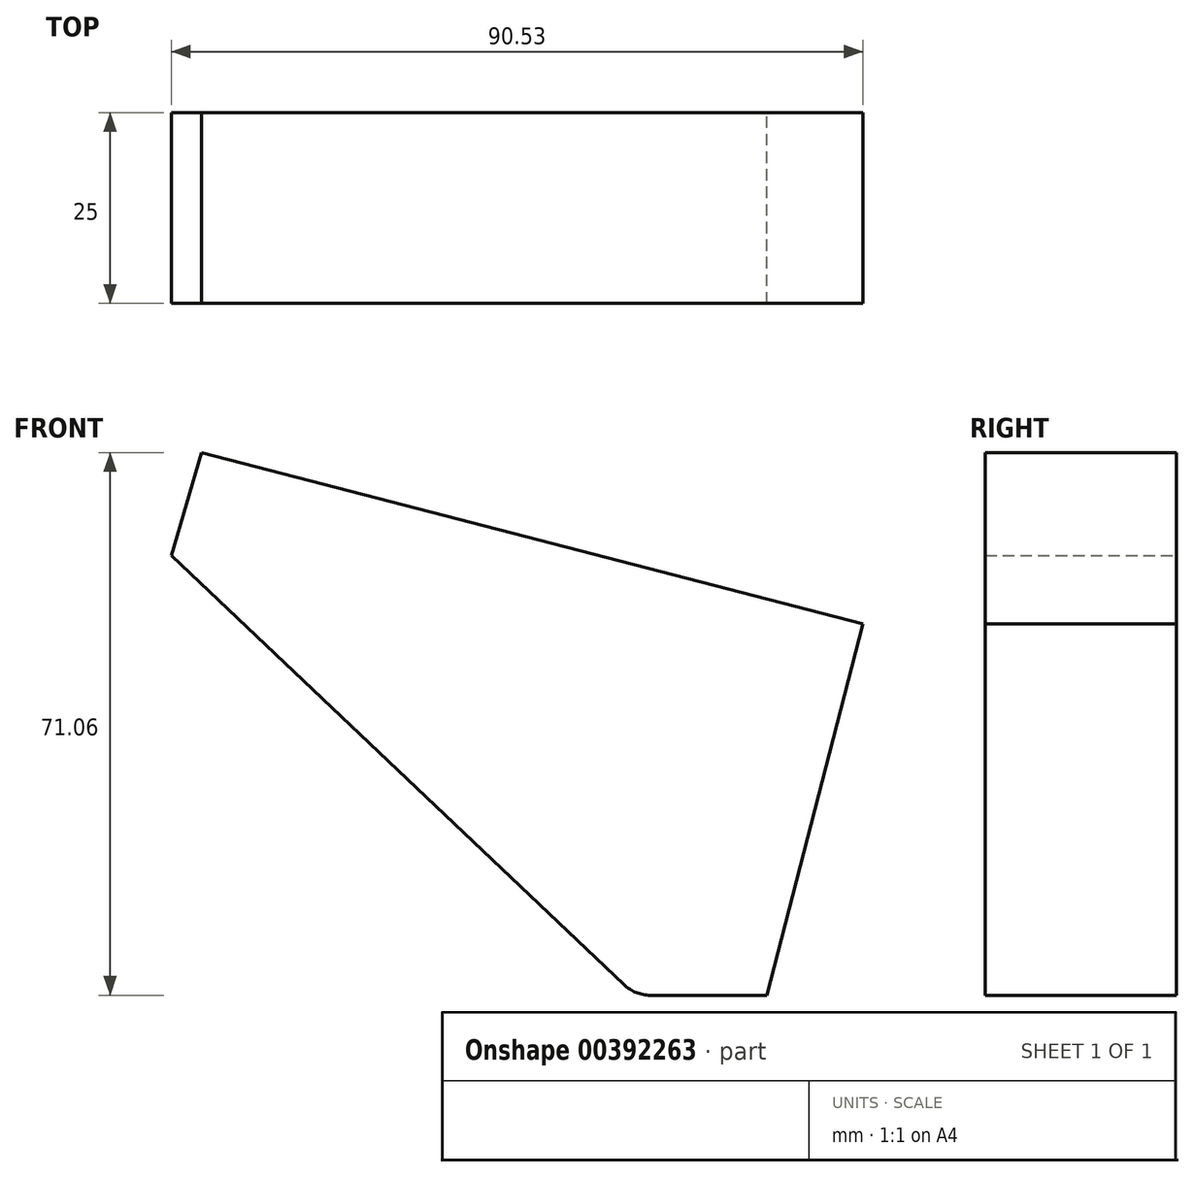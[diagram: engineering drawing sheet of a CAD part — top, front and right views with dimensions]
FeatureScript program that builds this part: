
annotation { "Feature Type Name" : "Feature", "Feature Type Description" : "" }
export const myFeature = defineFeature(function(context is Context, id is Id, definition is map)
    precondition{}
    {
        {
            var Q0;
            Q0=qCreatedBy(makeId("Front.planeOp"),FACE);
            var sketch = newSketch(context, id + "F0", { "sketchPlane" : qUnion([Q0])});
            skLineSegment(sketch, "E0", {"start": v(-106.78, 31.44) * mm, "end": v(-47.52, -24.78) * mm});
            skLineSegment(sketch, "E1", {"start": v(-44.08, -26.15) * mm, "end": v(36.91, -26.15) * mm});
            skLineSegment(sketch, "E2", {"start": v(47.27, -22) * mm, "end": v(63.82, -6.2) * mm});
            skLineSegment(sketch, "E3", {"start": v(61.62, 2.25) * mm, "end": v(-102.81, 44.9) * mm});
            skLineSegment(sketch, "E4", {"start": v(-102.81, 44.9) * mm, "end": v(-106.78, 31.44) * mm});
            skLineSegment(sketch, "E5", {"start": v(-16.25, 22.45) * mm, "end": v(-28.86, -26.15) * mm});
            skPoint(sketch, "E6.visualSharp", {"position": v(-46.08, -26.15) * mm});
            skArc(sketch, "E6.filletArc", {"start": v(-47.52, -24.78) * mm, "mid": v(-45.93, -25.8) * mm, "end": v(-44.08, -26.15) * mm});
            skPoint(sketch, "E7.visualSharp", {"position": v(42.92, -26.15) * mm});
            skArc(sketch, "E7.filletArc", {"start": v(36.91, -26.15) * mm, "mid": v(42.5, -25.08) * mm, "end": v(47.27, -22) * mm});
            skPoint(sketch, "E8.visualSharp", {"position": v(70.32, 0) * mm});
            skArc(sketch, "E8.filletArc", {"start": v(63.82, -6.2) * mm, "mid": v(65.2, -1.33) * mm, "end": v(61.62, 2.25) * mm});
            skSolve(sketch);
        }
        {
            var Q0;
            Q0=makeQuery(id+"F0.imprint","IMPRINT",FACE,{"disambiguationData":[TD([[makeQuery(id+"F0.imprint","IMPRINT",EDGE,{"derivedFrom":sQuery(id+"F0.wireOp",EDGE,"E0")}),1.0]])]});
            extrude(context, id + "F1", {"entities" : qUnion([Q0]), "depth" : 25 * mm});
        }
    });
